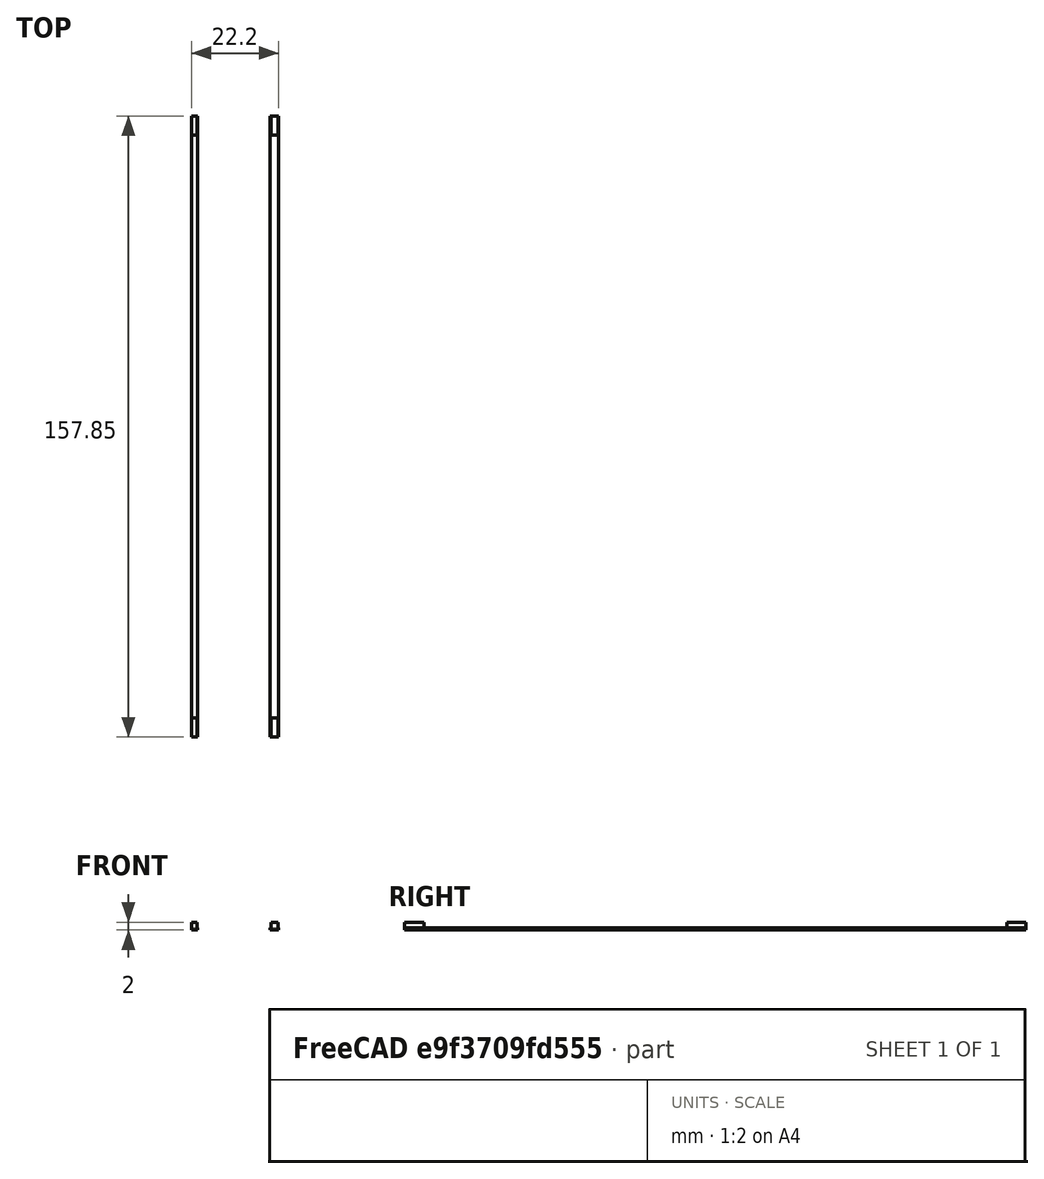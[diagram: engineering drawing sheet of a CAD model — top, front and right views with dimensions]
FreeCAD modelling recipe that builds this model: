
FCSTD DOCUMENT  (FreeCAD 0.17R13522 (Git))
Label: flejes_frente
License: CreativeCommons Attribution-ShareAlike
LicenseURL: http://creativecommons.org/licenses/by-sa/4.0/
objects: Part::Box×4, Part::Fuse×4, Part::Feature×2
note: 10 computed .brp shape members not serialized (recipe doc carries the construction recipe); baked Part::Feature solids carry a one-line shape summary decoded from their .brp

FEATURE [Part::Box] Box  label="fleje_angosto"
  AttacherType = Attacher::AttachEngine3D
  Height = 0.5
  Length = 1.6
  Width = 157.85
FEATURE [Part::Box] Box001  label="apoyo1"
  AttacherType = Attacher::AttachEngine3D
  Height = 2
  Length = 1.4
  Width = 4.9
FEATURE [Part::Feature] Box001001  label="apoyo002"
  Placement = pos=(0,152.95,0) rot=(0,0,1;0rad)
  shape: bbox 1.4 x 4.9 x 2 mm, 6 faces (baked)
FEATURE [Part::Fuse] Fusion
  Base = -> Box
  Refine = true
  Tool = -> Box001001
FEATURE [Part::Fuse] Fusion001  label="fleje_angosto_final"
  Base = -> Box001
  Refine = true
  Tool = -> Fusion
FEATURE [Part::Box] Box001002  label="fleje ancho sin soportes"
  AttacherType = Attacher::AttachEngine3D
  Height = 0.5
  Length = 2.2
  Placement = pos=(20,0,0) rot=(0,0,1;0rad)
  Width = 157.85
FEATURE [Part::Box] Box001003  label="apoyo003"
  AttacherType = Attacher::AttachEngine3D
  Height = 2
  Length = 1.8
  Placement = pos=(20.2,0,0) rot=(0,0,1;0rad)
  Width = 4.9
FEATURE [Part::Feature] Box001003002  label="apoyo005"
  Placement = pos=(20.2,152.95,0) rot=(0,0,1;0rad)
  shape: bbox 1.8 x 4.9 x 2 mm, 6 faces (baked)
FEATURE [Part::Fuse] Fusion002
  Base = -> Box001002
  Refine = true
  Tool = -> Box001003002
FEATURE [Part::Fuse] Fusion003  label="fleje_ancho_final"
  Base = -> Box001003
  Refine = true
  Tool = -> Fusion002
